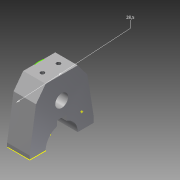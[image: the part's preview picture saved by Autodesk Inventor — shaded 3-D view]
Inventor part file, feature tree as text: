
AUTODESK INVENTOR PART (.ipt)
format: ipt  version: 2013 (Build 170138000, 138)  size: 1,552,384 bytes
history: native  units: mm
features: sketch x10, plane x2, hole x2, projected_geometry x2, extrude x1, other x1
ambient origin geometry x8: Origin, YZ Plane, XZ Plane, XY Plane, X Axis, Y Axis, Z Axis, Center Point
bodies: Solid1 (feature_tree)
feature tree (18):
  extrude  "Extrusion1"  Depth=22.0mm
  plane  "Work Plane1"
  sketch  "Sketch10"  dims[d21=9.0mm d26=10.0mm]
  sketch  "Sketch15"  dims[d50=5.0mm]
  hole  "Hole13"  [1 undecoded]
  plane  "Work Plane2"
  sketch  "Sketch17"  dims[d52=28.5mm d73=10.0mm d74=8.0mm d76=10.0mm d107=6.0mm d110=5.0mm d111=5.0mm d112=4.134mm d113=10.5mm d114=4.0mm d115=2.0mm d116=90.0deg d117=13.5mm d118=20.594885mm d119=6.0mm d120=12.5mm d122=14.0mm d123=2.459mm d124=6.5mm d125=4.0mm d126=2.0mm d127=90.0deg d128=6.5mm d129=20.594885mm d132=7.0mm d14=1.0mm d15=1.0mm]
  other  "Work Point4"
  hole  "Hole14"  [1 undecoded]
  sketch  "Sketch1"  dims[d0=8.0mm d2=22.0mm]
  sketch  "Sketch4"  dims[d3=14.0mm d4=20.0mm]
  sketch  "Sketch5"  dims[d5=10.0mm d9=14.0mm d10=4.5mm d11=0.0mm d12=0.698132mm]
  sketch  "Sketch8"  dims[d13=12.8mm]
  sketch  "Sketch13"  dims[d46=5.0mm]
  sketch  "Sketch14"  dims[d48=3.5mm]
  sketch  "Sketch16"  dims[d51=3.5mm]
  projected_geometry  "Projected Loop1"
  projected_geometry  "Projected Loop2"
note: 2 required parameter values undecoded (feature->parameter linkage not recoverable at this tier; creation-order binding heuristic only, values carry confidence <= 0.55)
